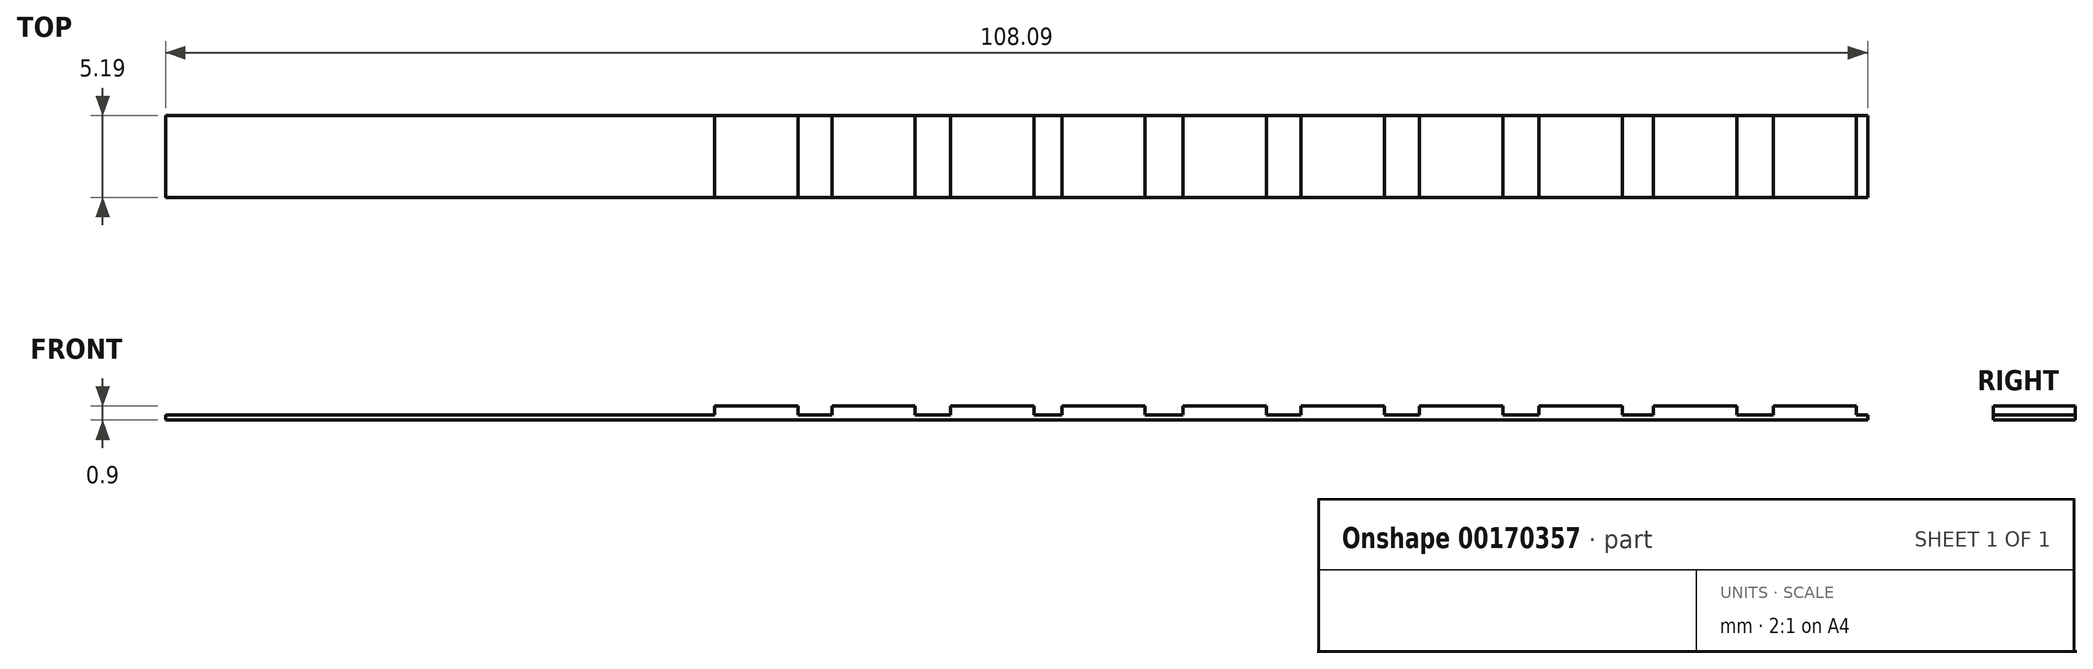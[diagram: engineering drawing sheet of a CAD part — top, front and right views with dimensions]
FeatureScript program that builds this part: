
annotation { "Feature Type Name" : "Feature", "Feature Type Description" : "" }
export const myFeature = defineFeature(function(context is Context, id is Id, definition is map)
    precondition{}
    {
        {
            var Q0;
            Q0=qCreatedBy(makeId("Front.planeOp"),FACE);
            var sketch = newSketch(context, id + "F0", { "sketchPlane" : qUnion([Q0])});
            skLineSegment(sketch, "E0.bottom", {"start": v(0, 0) * mm, "end": v(108.09, 0) * mm});
            skLineSegment(sketch, "E0.top", {"start": v(0, 0.32) * mm, "end": v(34.85, 0.32) * mm});
            skLineSegment(sketch, "E0.left", {"start": v(0, 0) * mm, "end": v(0, 0.32) * mm});
            skLineSegment(sketch, "E0.right", {"start": v(108.09, 0) * mm, "end": v(108.09, 0.32) * mm});
            skLineSegment(sketch, "E1.bottom", {"start": v(102.1, 0.9) * mm, "end": v(107.4, 0.9) * mm});
            skLineSegment(sketch, "E1.left", {"start": v(102.1, 0.9) * mm, "end": v(102.1, 0.32) * mm});
            skLineSegment(sketch, "E1.right", {"start": v(107.4, 0.9) * mm, "end": v(107.4, 0.32) * mm});
            skLineSegment(sketch, "E2.bottom", {"start": v(94.48, 0.9) * mm, "end": v(99.77, 0.9) * mm});
            skLineSegment(sketch, "E2.left", {"start": v(94.48, 0.9) * mm, "end": v(94.48, 0.32) * mm});
            skLineSegment(sketch, "E2.right", {"start": v(99.77, 0.9) * mm, "end": v(99.77, 0.32) * mm});
            skLineSegment(sketch, "E3.bottom", {"start": v(87.22, 0.9) * mm, "end": v(92.52, 0.9) * mm});
            skLineSegment(sketch, "E3.left", {"start": v(87.22, 0.9) * mm, "end": v(87.22, 0.32) * mm});
            skLineSegment(sketch, "E3.right", {"start": v(92.52, 0.9) * mm, "end": v(92.52, 0.32) * mm});
            skLineSegment(sketch, "E4.bottom", {"start": v(79.63, 0.9) * mm, "end": v(84.92, 0.9) * mm});
            skLineSegment(sketch, "E4.left", {"start": v(79.63, 0.9) * mm, "end": v(79.63, 0.32) * mm});
            skLineSegment(sketch, "E4.right", {"start": v(84.92, 0.9) * mm, "end": v(84.92, 0.32) * mm});
            skLineSegment(sketch, "E5.bottom", {"start": v(72.1, 0.9) * mm, "end": v(77.4, 0.9) * mm});
            skLineSegment(sketch, "E5.left", {"start": v(72.1, 0.9) * mm, "end": v(72.1, 0.32) * mm});
            skLineSegment(sketch, "E5.right", {"start": v(77.4, 0.9) * mm, "end": v(77.4, 0.32) * mm});
            skLineSegment(sketch, "E6.bottom", {"start": v(64.62, 0.9) * mm, "end": v(69.91, 0.9) * mm});
            skLineSegment(sketch, "E6.left", {"start": v(64.62, 0.9) * mm, "end": v(64.62, 0.32) * mm});
            skLineSegment(sketch, "E6.right", {"start": v(69.91, 0.9) * mm, "end": v(69.91, 0.32) * mm});
            skLineSegment(sketch, "E7.bottom", {"start": v(56.9, 0.9) * mm, "end": v(62.2, 0.9) * mm});
            skLineSegment(sketch, "E7.left", {"start": v(56.9, 0.9) * mm, "end": v(56.9, 0.32) * mm});
            skLineSegment(sketch, "E7.right", {"start": v(62.2, 0.9) * mm, "end": v(62.2, 0.32) * mm});
            skLineSegment(sketch, "E8.bottom", {"start": v(49.83, 0.9) * mm, "end": v(55.13, 0.9) * mm});
            skLineSegment(sketch, "E8.left", {"start": v(49.83, 0.9) * mm, "end": v(49.83, 0.32) * mm});
            skLineSegment(sketch, "E8.right", {"start": v(55.13, 0.9) * mm, "end": v(55.13, 0.32) * mm});
            skLineSegment(sketch, "E9.bottom", {"start": v(42.3, 0.9) * mm, "end": v(47.6, 0.9) * mm});
            skLineSegment(sketch, "E9.left", {"start": v(42.3, 0.9) * mm, "end": v(42.3, 0.32) * mm});
            skLineSegment(sketch, "E9.right", {"start": v(47.6, 0.9) * mm, "end": v(47.6, 0.32) * mm});
            skLineSegment(sketch, "E10.bottom", {"start": v(34.85, 0.9) * mm, "end": v(40.14, 0.9) * mm});
            skLineSegment(sketch, "E10.left", {"start": v(34.85, 0.9) * mm, "end": v(34.85, 0.32) * mm});
            skLineSegment(sketch, "E10.right", {"start": v(40.14, 0.9) * mm, "end": v(40.14, 0.32) * mm});
            skLineSegment(sketch, "E11.trimOffspring", {"start": v(107.4, 0.32) * mm, "end": v(108.09, 0.32) * mm});
            skLineSegment(sketch, "E12.trimOffspring", {"start": v(99.77, 0.32) * mm, "end": v(102.1, 0.32) * mm});
            skLineSegment(sketch, "E13.trimOffspring", {"start": v(92.52, 0.32) * mm, "end": v(94.48, 0.32) * mm});
            skLineSegment(sketch, "E14.trimOffspring", {"start": v(84.92, 0.32) * mm, "end": v(87.22, 0.32) * mm});
            skLineSegment(sketch, "E15.trimOffspring", {"start": v(77.4, 0.32) * mm, "end": v(79.63, 0.32) * mm});
            skLineSegment(sketch, "E16.trimOffspring", {"start": v(69.91, 0.32) * mm, "end": v(72.1, 0.32) * mm});
            skLineSegment(sketch, "E17.trimOffspring", {"start": v(62.2, 0.32) * mm, "end": v(64.62, 0.32) * mm});
            skLineSegment(sketch, "E18.trimOffspring", {"start": v(55.13, 0.32) * mm, "end": v(56.9, 0.32) * mm});
            skLineSegment(sketch, "E19.trimOffspring", {"start": v(47.6, 0.32) * mm, "end": v(49.83, 0.32) * mm});
            skLineSegment(sketch, "E20.trimOffspring", {"start": v(40.14, 0.32) * mm, "end": v(42.3, 0.32) * mm});
            skSolve(sketch);
        }
        {
            var Q0;
            Q0 = qSketchRegion(id + "F0", true);
            extrude(context, id + "F1", {"entities" : qUnion([Q0]), "depth" : 5.2 * mm});
        }
    });
